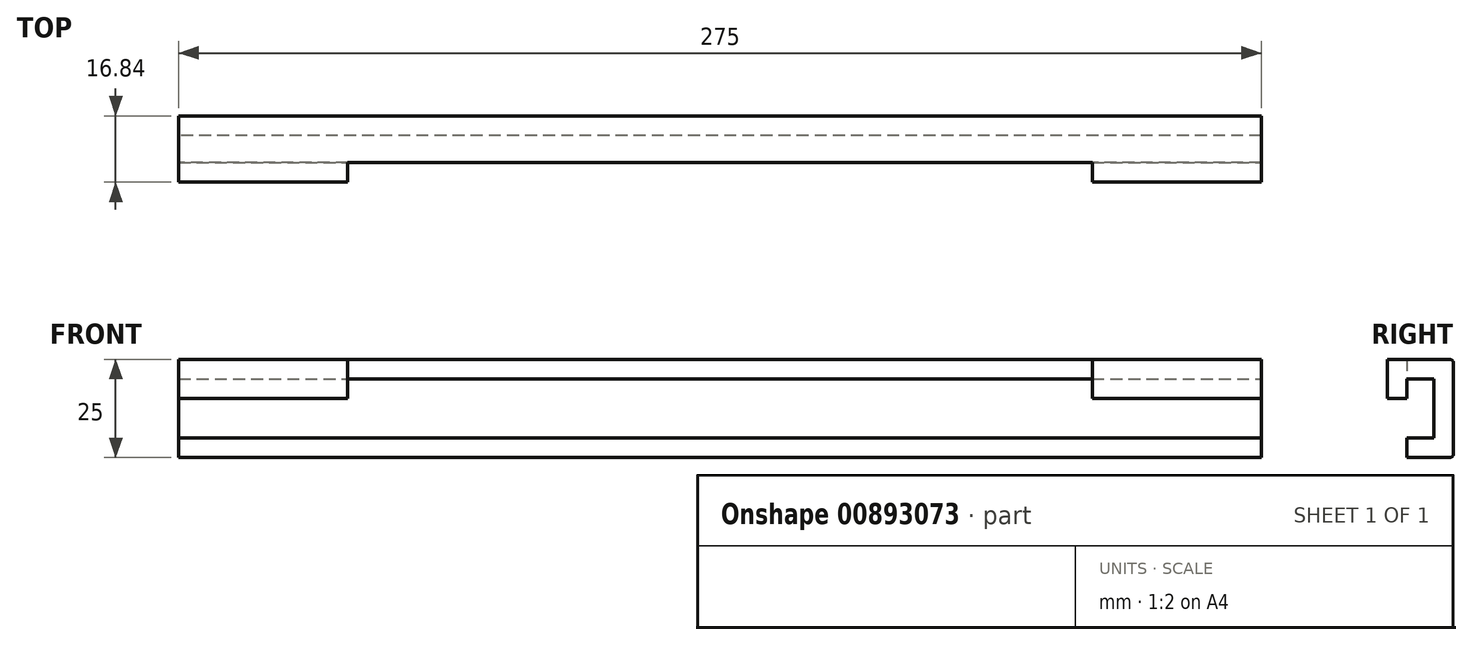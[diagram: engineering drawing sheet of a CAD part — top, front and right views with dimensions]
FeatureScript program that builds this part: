
annotation { "Feature Type Name" : "Feature", "Feature Type Description" : "" }
export const myFeature = defineFeature(function(context is Context, id is Id, definition is map)
    precondition{}
    {
        {
            var Q0;
            Q0=qCreatedBy(makeId("Top.planeOp"),FACE);
            var sketch = newSketch(context, id + "F0", { "sketchPlane" : qUnion([Q0])});
            skLineSegment(sketch, "E0.bottom", {"start": v(137.5, 2.5) * mm, "end": v(-137.5, 2.5) * mm});
            skLineSegment(sketch, "E0.top", {"start": v(137.5, -2.5) * mm, "end": v(-137.5, -2.5) * mm});
            skLineSegment(sketch, "E0.left", {"start": v(137.5, 2.5) * mm, "end": v(137.5, -2.5) * mm});
            skLineSegment(sketch, "E0.right", {"start": v(-137.5, 2.5) * mm, "end": v(-137.5, -2.5) * mm});
            skPoint(sketch, "E0.middle", {"position": v(0, 0) * mm});
            skSolve(sketch);
        }
        {
            var Q0;
            Q0 = qSketchRegion(id + "F0", true);
            extrude(context, id + "F1", {"entities" : qUnion([Q0]), "endBound" : BoundingType.SYMMETRIC, "depth" : 15 * mm, "offsetDistance" : 25 * mm});
        }
        {
            var Q0;
            Q0=makeQuery(id+"F1.opExtrude","CAP_FACE",FACE,{"disambiguationData":[OSD([sQuery(id+"F0.wireOp",EDGE,"E0.bottom"),sQuery(id+"F0.wireOp",EDGE,"E0.top"),sQuery(id+"F0.wireOp",EDGE,"E0.left"),sQuery(id+"F0.wireOp",EDGE,"E0.right")])],"isStart":false});
            var sketch = newSketch(context, id + "F2", { "sketchPlane" : qUnion([Q0])});
            skLineSegment(sketch, "E1.bottom", {"start": v(-137.5, 2.5) * mm, "end": v(137.5, 2.5) * mm});
            skLineSegment(sketch, "E1.top", {"start": v(-137.5, -9.34) * mm, "end": v(137.5, -9.34) * mm});
            skLineSegment(sketch, "E1.left", {"start": v(-137.5, 2.5) * mm, "end": v(-137.5, -9.34) * mm});
            skLineSegment(sketch, "E1.right", {"start": v(137.5, 2.5) * mm, "end": v(137.5, -9.34) * mm});
            skSolve(sketch);
        }
        {
            var Q0;
            Q0 = qSketchRegion(id + "F2", true);
            extrude(context, id + "F3", {"entities" : qUnion([Q0]), "operationType" : NewBodyOperationType.ADD, "depth" : 5 * mm, "offsetDistance" : 25 * mm});
        }
        {
            var Q0;
            Q0=makeQuery(id+"F3.opExtrude","SWEPT_FACE",FACE,{"disambiguationData":[OSD([sQuery(id+"F2.wireOp",EDGE,"E1.top")])]});
            var sketch = newSketch(context, id + "F4", { "sketchPlane" : qUnion([Q0])});
            skLineSegment(sketch, "E2.bottom", {"start": v(-137.5, 12.5) * mm, "end": v(-94.6, 12.5) * mm});
            skLineSegment(sketch, "E2.top", {"start": v(-137.5, 2.5) * mm, "end": v(-94.6, 2.5) * mm});
            skLineSegment(sketch, "E2.left", {"start": v(-137.5, 12.5) * mm, "end": v(-137.5, 2.5) * mm});
            skLineSegment(sketch, "E2.right", {"start": v(137.5, 12.5) * mm, "end": v(137.5, 2.5) * mm});
            skLineSegment(sketch, "E3.left", {"start": v(-94.6, 12.5) * mm, "end": v(-94.6, 2.5) * mm});
            skLineSegment(sketch, "E3.right", {"start": v(94.6, 12.5) * mm, "end": v(94.6, 2.5) * mm});
            skPoint(sketch, "E3.middle", {"position": v(0, 0) * mm});
            skLineSegment(sketch, "E4.trimOffspring", {"start": v(94.6, 2.5) * mm, "end": v(137.5, 2.5) * mm});
            skLineSegment(sketch, "E5.trimOffspring", {"start": v(94.6, 12.5) * mm, "end": v(137.5, 12.5) * mm});
            skPoint(sketch, "E3.top.start.orphan", {"position": v(-94.6, -32.66) * mm});
            skPoint(sketch, "E3.bottom.start.orphan", {"position": v(-94.6, 32.66) * mm});
            skPoint(sketch, "E6.orphan", {"position": v(94.6, 32.66) * mm});
            skPoint(sketch, "E7.orphan", {"position": v(94.6, -32.66) * mm});
            skSolve(sketch);
        }
        {
            var Q0;
            Q0 = qSketchRegion(id + "F4", true);
            extrude(context, id + "F5", {"entities" : qUnion([Q0]), "operationType" : NewBodyOperationType.ADD, "depth" : 5 * mm, "offsetDistance" : 25 * mm});
        }
        {
            var Q0;
            Q0=makeQuery(id+"F1.opExtrude","CAP_FACE",FACE,{"disambiguationData":[OSD([sQuery(id+"F0.wireOp",EDGE,"E0.bottom"),sQuery(id+"F0.wireOp",EDGE,"E0.top"),sQuery(id+"F0.wireOp",EDGE,"E0.left"),sQuery(id+"F0.wireOp",EDGE,"E0.right")])],"isStart":true});
            var sketch = newSketch(context, id + "F6", { "sketchPlane" : qUnion([Q0])});
            skLineSegment(sketch, "E8.bottom", {"start": v(137.5, -2.5) * mm, "end": v(-137.5, -2.5) * mm});
            skLineSegment(sketch, "E8.top", {"start": v(137.5, 9.39) * mm, "end": v(-137.5, 9.39) * mm});
            skLineSegment(sketch, "E8.left", {"start": v(137.5, -2.5) * mm, "end": v(137.5, 9.39) * mm});
            skLineSegment(sketch, "E8.right", {"start": v(-137.5, -2.5) * mm, "end": v(-137.5, 9.39) * mm});
            skSolve(sketch);
        }
        {
            var Q0;
            Q0 = qSketchRegion(id + "F6", true);
            extrude(context, id + "F7", {"entities" : qUnion([Q0]), "operationType" : NewBodyOperationType.ADD, "depth" : 5 * mm, "offsetDistance" : 25 * mm});
        }
        {
            var Q0;
            Q0=makeQuery(id+"F3.opExtrude","CAP_EDGE",EDGE,{"disambiguationData":[OSD([sQuery(id+"F2.wireOp",EDGE,"E1.bottom")])],"isStart":false});
            var Q1;
            Q1=makeQuery(id+"F7.opExtrude","CAP_EDGE",EDGE,{"disambiguationData":[OSD([sQuery(id+"F6.wireOp",EDGE,"E8.bottom")])],"isStart":false});
            fillet(context, id + "F8", {"entities" : qUnion([Q0, Q1]), "radius" : 1 * mm, "tangentPropagation" : true, "allowEdgeOverflow" : false});
        }
    });
